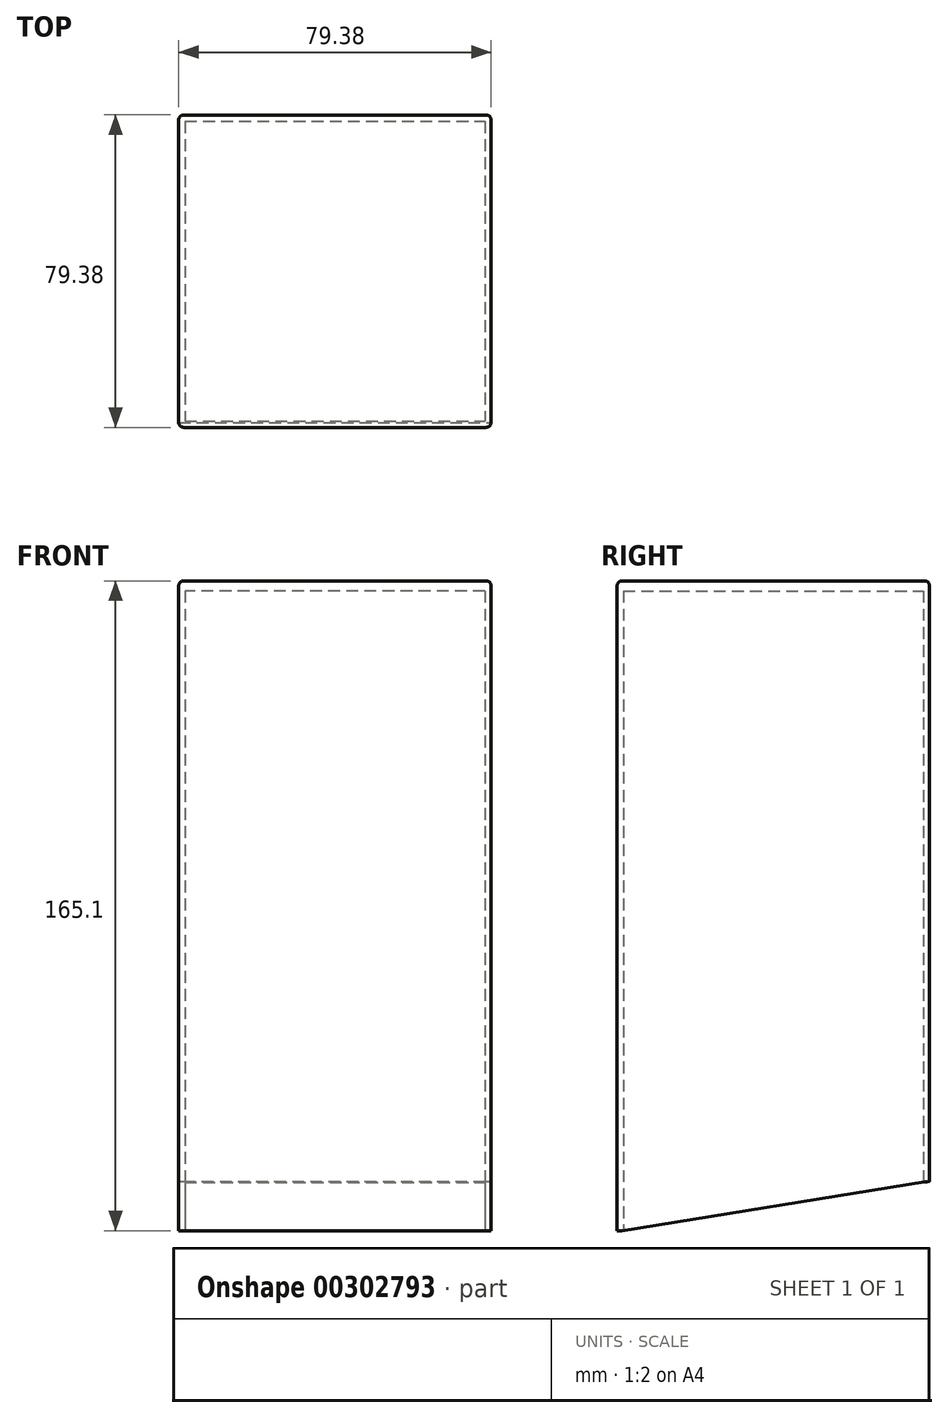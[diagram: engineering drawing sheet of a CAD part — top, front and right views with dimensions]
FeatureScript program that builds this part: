
annotation { "Feature Type Name" : "Feature", "Feature Type Description" : "" }
export const myFeature = defineFeature(function(context is Context, id is Id, definition is map)
    precondition{}
    {
        {
            var Q0;
            Q0=qCreatedBy(makeId("Top.planeOp"),FACE);
            var sketch = newSketch(context, id + "F0", { "sketchPlane" : qUnion([Q0])});
            skLineSegment(sketch, "E0.bottom", {"start": v(39.69, 39.69) * mm, "end": v(-39.69, 39.69) * mm});
            skLineSegment(sketch, "E0.top", {"start": v(39.69, -39.69) * mm, "end": v(-39.69, -39.69) * mm});
            skLineSegment(sketch, "E0.left", {"start": v(39.69, 39.69) * mm, "end": v(39.69, -39.69) * mm});
            skLineSegment(sketch, "E0.right", {"start": v(-39.69, 39.69) * mm, "end": v(-39.69, -39.69) * mm});
            skPoint(sketch, "E0.middle", {"position": v(0, 0) * mm});
            skSolve(sketch);
        }
        {
            var Q0;
            Q0 = qSketchRegion(id + "F0", true);
            extrude(context, id + "F1", {"entities" : qUnion([Q0]), "depth" : 165.1 * mm});
        }
        {
            var Q0;
            Q0=makeQuery(id+"F1.opExtrude","CAP_FACE",FACE,{"disambiguationData":[OSD([sQuery(id+"F0.wireOp",EDGE,"E0.bottom"),sQuery(id+"F0.wireOp",EDGE,"E0.top"),sQuery(id+"F0.wireOp",EDGE,"E0.left"),sQuery(id+"F0.wireOp",EDGE,"E0.right")])],"isStart":true});
            var sketch = newSketch(context, id + "F2", { "sketchPlane" : qUnion([Q0])});
            skLineSegment(sketch, "E1.bottom", {"start": v(38.1, 38.1) * mm, "end": v(-38.1, 38.1) * mm});
            skLineSegment(sketch, "E1.top", {"start": v(38.1, -38.1) * mm, "end": v(-38.1, -38.1) * mm});
            skLineSegment(sketch, "E1.left", {"start": v(38.1, 38.1) * mm, "end": v(38.1, -38.1) * mm});
            skLineSegment(sketch, "E1.right", {"start": v(-38.1, 38.1) * mm, "end": v(-38.1, -38.1) * mm});
            skPoint(sketch, "E1.middle", {"position": v(0, 0) * mm});
            skSolve(sketch);
        }
        {
            var Q0;
            Q0 = qSketchRegion(id + "F2", true);
            extrude(context, id + "F3", {"entities" : qUnion([Q0]), "operationType" : NewBodyOperationType.REMOVE, "oppositeDirection" : true, "depth" : 162.56 * mm});
        }
        {
            var Q0;
            Q0=makeQuery(id+"F1.opExtrude","SWEPT_EDGE",EDGE,{"disambiguationData":[OSD([sQuery(id+"F0.wireOp",EDGE,"E0.top"),sQuery(id+"F0.wireOp",EDGE,"E0.left")])]});
            var Q1;
            Q1=makeQuery(id+"F1.opExtrude","CAP_EDGE",EDGE,{"disambiguationData":[OSD([sQuery(id+"F0.wireOp",EDGE,"E0.left")])],"isStart":false});
            var Q2;
            Q2=makeQuery(id+"F1.opExtrude","SWEPT_EDGE",EDGE,{"disambiguationData":[OSD([sQuery(id+"F0.wireOp",EDGE,"E0.bottom"),sQuery(id+"F0.wireOp",EDGE,"E0.left")])]});
            var Q3;
            Q3=makeQuery(id+"F1.opExtrude","SWEPT_EDGE",EDGE,{"disambiguationData":[OSD([sQuery(id+"F0.wireOp",EDGE,"E0.top"),sQuery(id+"F0.wireOp",EDGE,"E0.right")])]});
            var Q4;
            Q4=makeQuery(id+"F1.opExtrude","CAP_EDGE",EDGE,{"disambiguationData":[OSD([sQuery(id+"F0.wireOp",EDGE,"E0.top")])],"isStart":false});
            var Q5;
            Q5=makeQuery(id+"F1.opExtrude","CAP_EDGE",EDGE,{"disambiguationData":[OSD([sQuery(id+"F0.wireOp",EDGE,"E0.bottom")])],"isStart":false});
            var Q6;
            Q6=makeQuery(id+"F1.opExtrude","SWEPT_EDGE",EDGE,{"disambiguationData":[OSD([sQuery(id+"F0.wireOp",EDGE,"E0.bottom"),sQuery(id+"F0.wireOp",EDGE,"E0.right")])]});
            var Q7;
            Q7=makeQuery(id+"F1.opExtrude","CAP_EDGE",EDGE,{"disambiguationData":[OSD([sQuery(id+"F0.wireOp",EDGE,"E0.right")])],"isStart":false});
            fillet(context, id + "F4", {"entities" : qUnion([Q0, Q1, Q2, Q3, Q4, Q5, Q6, Q7]), "radius" : 1.27 * mm, "tangentPropagation" : true, "allowEdgeOverflow" : false});
        }
        {
            var Q0;
            Q0=makeQuery(id+"F1.opExtrude","SWEPT_FACE",FACE,{"disambiguationData":[OSD([sQuery(id+"F0.wireOp",EDGE,"E0.left")])]});
            var sketch = newSketch(context, id + "F5", { "sketchPlane" : qUnion([Q0])});
            skLineSegment(sketch, "E2", {"start": v(-38.42, 0) * mm, "end": v(46.89, 13.7) * mm});
            skLineSegment(sketch, "E3", {"start": v(46.89, 13.7) * mm, "end": v(46.89, -9.38) * mm});
            skLineSegment(sketch, "E4", {"start": v(46.89, -9.38) * mm, "end": v(-38.42, 0) * mm});
            skSolve(sketch);
        }
        {
            var Q0;
            Q0 = qSketchRegion(id + "F5", true);
            extrude(context, id + "F6", {"entities" : qUnion([Q0]), "operationType" : NewBodyOperationType.REMOVE, "endBound" : BoundingType.THROUGH_ALL, "oppositeDirection" : true, "depth" : 25.4 * mm});
        }
    });
